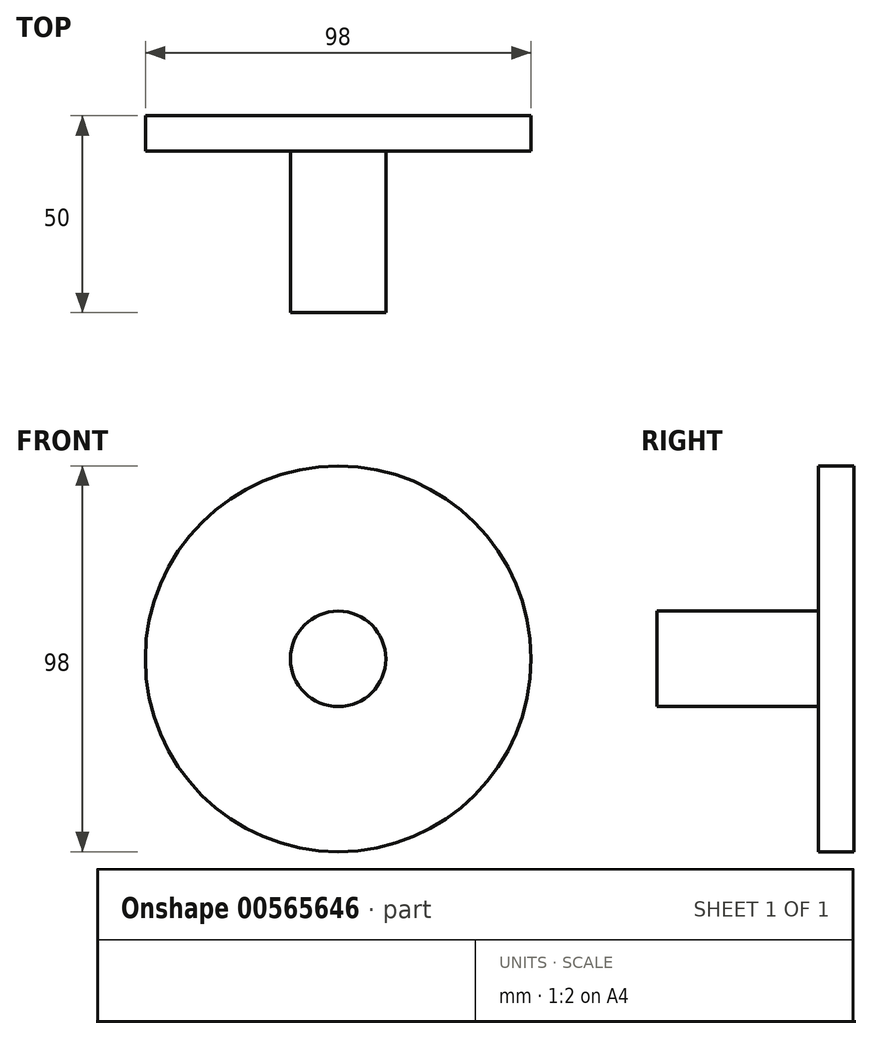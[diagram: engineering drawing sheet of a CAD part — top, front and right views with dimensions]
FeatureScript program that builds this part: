
annotation { "Feature Type Name" : "Feature", "Feature Type Description" : "" }
export const myFeature = defineFeature(function(context is Context, id is Id, definition is map)
    precondition{}
    {
        {
            var Q0;
            Q0=qCreatedBy(makeId("Front.planeOp"),FACE);
            var sketch = newSketch(context, id + "F0", { "sketchPlane" : qUnion([Q0])});
            skCircle(sketch, "E0", {"center": v(0, 0) * mm, "radius": 49 * mm});
            skCircle(sketch, "E1", {"center": v(0, 0) * mm, "radius": 12.12 * mm});
            skSolve(sketch);
        }
        {
            var Q0;
            Q0=makeQuery(id+"F0.imprint","IMPRINT",FACE,{"disambiguationData":[TD([[makeQuery(id+"F0.imprint","IMPRINT",EDGE,{"derivedFrom":sQuery(id+"F0.wireOp",EDGE,"E0")}),1.0]])]});
            var Q1;
            Q1=makeQuery(id+"F0.imprint","IMPRINT",FACE,{"disambiguationData":[TD([[makeQuery(id+"F0.imprint","IMPRINT",EDGE,{"derivedFrom":sQuery(id+"F0.wireOp",EDGE,"E1")}),1.0]])]});
            extrude(context, id + "F1", {"entities" : qUnion([Q0, Q1]), "depth" : 9 * mm, "offsetDistance" : 25 * mm});
        }
        {
            var Q0;
            Q0=makeQuery(id+"F0.imprint","IMPRINT",FACE,{"disambiguationData":[TD([[makeQuery(id+"F0.imprint","IMPRINT",EDGE,{"derivedFrom":sQuery(id+"F0.wireOp",EDGE,"E1")}),1.0]])]});
            extrude(context, id + "F2", {"entities" : qUnion([Q0]), "operationType" : NewBodyOperationType.ADD, "depth" : 50 * mm, "offsetDistance" : 25 * mm});
        }
    });
